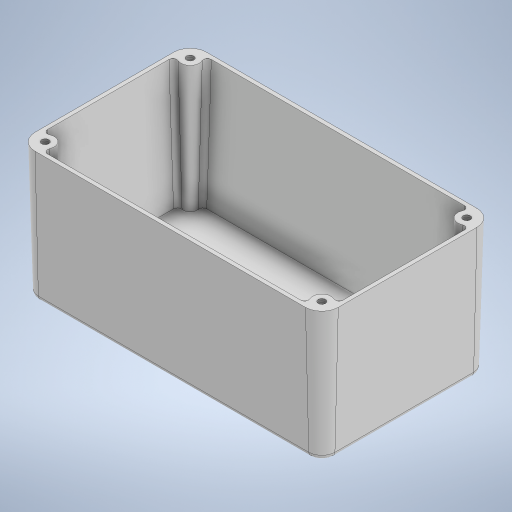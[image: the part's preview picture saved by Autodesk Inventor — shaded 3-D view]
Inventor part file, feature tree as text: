
AUTODESK INVENTOR PART (.ipt)
format: ipt  version: 2023 (Build 270158030, 158C)  size: 507,392 bytes
history: native  units: mm
features: sketch x8, extrude x6, other x4, fillet x3, hole x2, plane x1
ambient origin geometry x8: Origin, YZ Plane, XZ Plane, XY Plane, X Axis, Y Axis, Z Axis, Center Point
bodies: Body1 (feature_tree), Body2 (feature_tree)
feature tree (24):
  other  "Die Cast Box"
  other  "Annotations"
  extrude  "Extrusion1"  Depth=63.6mm
  sketch  "Sketch2"  dims[d2=5.0mm d10=51.1mm d11=0.261799mm]
  plane  "Work Plane1"
  extrude  "Extrusion2"  Depth=5.0mm
  extrude  "Extrusion3"  Depth=1.5mm
  fillet  "Fillet1"  Radius=1.5mm
  sketch  "Sketch4"  dims[d16=4.0mm d17=-1.5mm d18=51.1mm d19=-0.261799mm]
  fillet  "Fillet2"  Radius=1.5mm
  hole  "Hole1"  [1 undecoded]
  extrude  "Extrusion4"  Depth=4.0mm
  fillet  "Fillet3"  Radius=5.3mm
  hole  "Hole2"  [1 undecoded]
  extrude  "Extrusion5"  Depth=3.8mm
  extrude  "Extrusion6"  Depth=1.5mm
  sketch  "Sketch1"  dims[d0=114.5mm d1=63.6mm]
  sketch  "Sketch3"  dims[d12=1.5mm d13=1.5mm d14=1.5mm d15=1.5mm]
  sketch  "Sketch5"  dims[d20=4.0mm d21=4.0mm d22=5.3mm]
  other  "Die Cast Lid"
  sketch  "Sketch6"  dims[d23=3.8mm d24=3.8mm]
  sketch  "Sketch7"  dims[d25=3.8mm d26=3.8mm]
  sketch  "Sketch8"  dims[d27=10.0mm d28=0.174533mm d29=1.5mm d30=3.0mm d31=2.0mm d32=2.85mm d33=7.0mm d34=4.0mm d35=2.0mm d36=90.0deg d37=20.0mm d38=20.594885mm d39=5.67mm d40=4.0mm d41=0.0mm d42=1.5mm d43=3.0mm d44=3.0mm d45=7.0mm d46=4.0mm d47=2.0mm d48=90.0deg d49=4.0mm d50=20.594885mm d51=0.5mm d52=0.5mm d53=0.5mm d54=0.5mm d55=1.5mm d56=1.5mm d57=1.5mm d58=1.5mm d59=0.5mm d60=0.5mm d62=10.0mm d63=10.0mm d64=10.0mm d65=10.0mm d66=2.5mm d67=0.0mm d71=9.0mm d72=9.0mm d73=9.0mm d74=9.0mm d75=1.0mm d76=2.5mm d77=0.0mm]
  other  "General Note 1"
note: 2 required parameter values undecoded (feature->parameter linkage not recoverable at this tier; creation-order binding heuristic only, values carry confidence <= 0.55)
